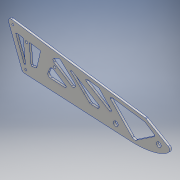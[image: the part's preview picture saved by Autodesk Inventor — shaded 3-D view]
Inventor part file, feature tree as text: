
AUTODESK INVENTOR PART (.ipt)
format: ipt  version: 2018.2 (Build 222227000, 227)  size: 1,334,272 bytes
history: native  units: mm
features: extrude x4, sketch x4, projected_geometry x2, fillet x1
ambient origin geometry x8: Origin, YZ Plane, XZ Plane, XY Plane, X Axis, Y Axis, Z Axis, Center Point
bodies: Body1 (feature_tree)
feature tree (11):
  extrude  "押し出し3"  TaperAngle=30.0deg  [1 undecoded]
  fillet  "フィレット2"  Radius=5.0mm
  sketch  "スケッチ4"
  extrude  "押し出し7"  Depth=6.0mm
  extrude  "押し出し9"  Depth=5.0mm
  extrude  "押し出し13"  Depth=10.0mm
  sketch  "スケッチ2"
  projected_geometry  "投影ループ4"
  projected_geometry  "投影ループ5"
  sketch  "スケッチ6"
  sketch  "スケッチ10"
note: 1 required parameter value undecoded (feature->parameter linkage not recoverable at this tier; creation-order binding heuristic only, values carry confidence <= 0.55)
